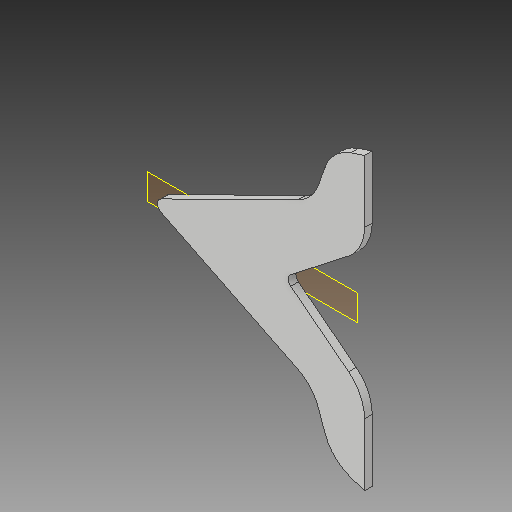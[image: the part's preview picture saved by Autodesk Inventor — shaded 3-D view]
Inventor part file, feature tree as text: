
AUTODESK INVENTOR PART (.ipt)
format: ipt  version: 2017 (Build 210142000, 142)  size: 130,048 bytes
history: native  units: mm
features: other x3, fillet x2, plane x1, extrude x1, mirror x1, sketch x1
ambient origin geometry x8: Origin, YZ Plane, XZ Plane, XY Plane, X Axis, Y Axis, Z Axis, Center Point
bodies: Solid1 (feature_tree)
feature tree (9):
  plane  "Work Plane1"
  extrude  "Extrusion1"  Depth=8.25mm
  mirror  "Mirror1"
  fillet  "Fillet1"  Radius=54.25mm
  fillet  "Fillet2"  [1 undecoded]
  sketch  "Sketch1"  dims[d0=10.0mm d1=0.0mm d2=8.25mm d3=54.25mm]
  other  "<userpath>\Desktop\asa1\assembly.iam"
  other  "assembly.iam"
  other  "Part1:1"
note: 1 required parameter value undecoded (feature->parameter linkage not recoverable at this tier; creation-order binding heuristic only, values carry confidence <= 0.55)
